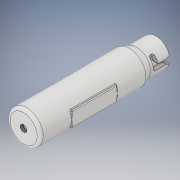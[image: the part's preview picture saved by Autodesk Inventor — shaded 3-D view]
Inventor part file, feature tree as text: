
AUTODESK INVENTOR PART (.ipt)
format: ipt  version: 2019 (Build 230136000, 136)  size: 1,455,616 bytes
history: native  units: mm
features: other x10, sketch x6, fillet x5, extrude x3, chamfer x3, pattern_circular x1, mirror x1
ambient origin geometry x8: Origin, YZ Plane, XZ Plane, XY Plane, X Axis, Y Axis, Z Axis, Center Point
bodies: Solide1 (feature_tree)
feature tree (29):
  other  "Révolution1"
  other  "Plan de construction1"
  extrude  "Extrusion1"  Depth=4.0mm
  other  "Hélicoïde1"
  extrude  "Extrusion2"  Depth=20.0mm
  fillet  "Congé1"  Radius=4.0mm
  fillet  "Congé2"  Radius=0.25mm
  fillet  "Congé3"  Radius=20.0mm
  chamfer  "Chanfrein1"  Distance=130.0mm
  chamfer  "Chanfrein2"  Distance=0.25mm
  pattern_circular  "Réseau circulaire3"  [2 undecoded]
  chamfer  "Chanfrein5"  Distance=6.0mm
  other  "Plan de construction3"
  extrude  "Extrusion5"  Depth=0.25mm
  fillet  "Congé5"  Radius=10.5mm
  fillet  "Congé6"  Radius=6.0mm
  mirror  "Symétrie1"
  other  "Plan de construction6"
  other  "Gravure2"
  sketch  "Esquisse1"
  sketch  "Esquisse2"
  sketch  "Esquisse4"
  sketch  "Esquisse5"
  sketch  "Esquisse12"
  sketch  "Esquisse18"
  other  "Projeter les arêtes coupées1"
  other  "Projeter les arêtes coupées4"
  other  "Projeter les arêtes coupées5"
  other  "Projeter les arêtes coupées6"
note: 2 required parameter values undecoded (feature->parameter linkage not recoverable at this tier; creation-order binding heuristic only, values carry confidence <= 0.55)
